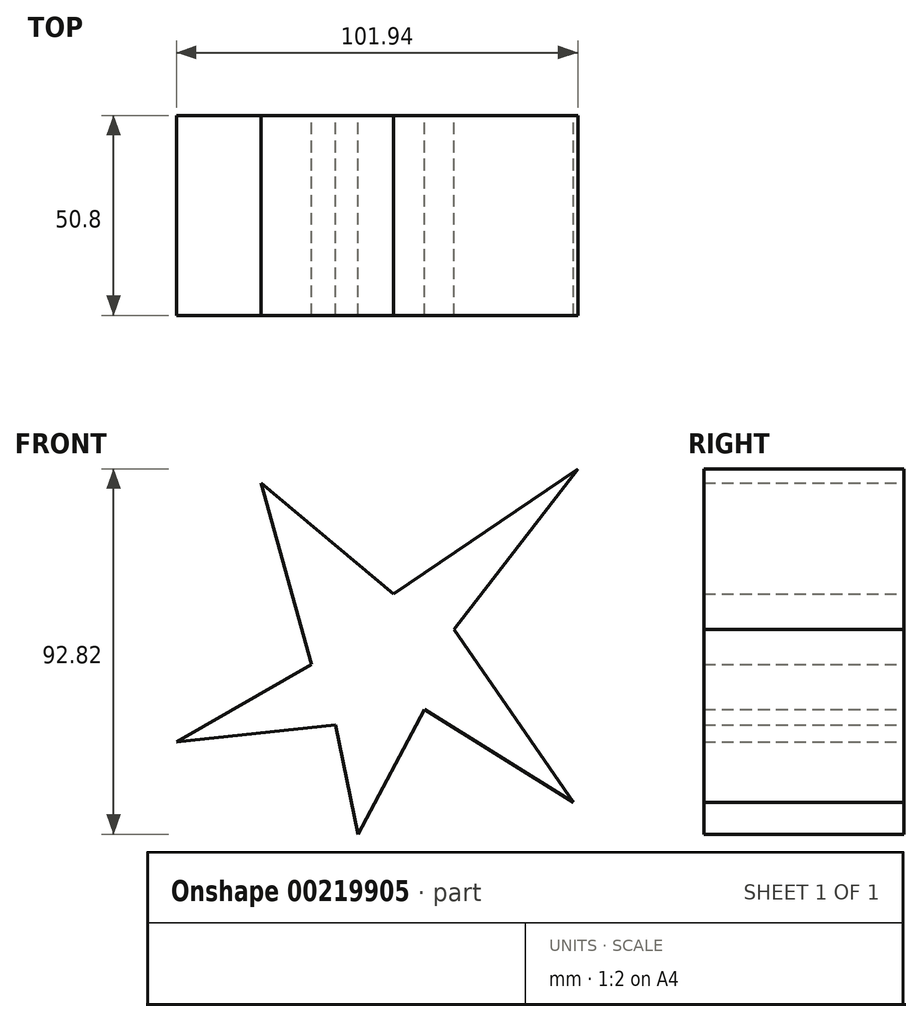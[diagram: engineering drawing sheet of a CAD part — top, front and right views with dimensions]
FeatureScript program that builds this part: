
annotation { "Feature Type Name" : "Feature", "Feature Type Description" : "" }
export const myFeature = defineFeature(function(context is Context, id is Id, definition is map)
    precondition{}
    {
        {
            var Q0;
            Q0=qCreatedBy(makeId("Front.planeOp"),FACE);
            var sketch = newSketch(context, id + "F0", { "sketchPlane" : qUnion([Q0])});
            skLineSegment(sketch, "E0", {"start": v(0, 0) * mm, "end": v(16.81, 31.66) * mm});
            skLineSegment(sketch, "E1", {"start": v(16.81, 31.66) * mm, "end": v(54.73, 8.05) * mm});
            skLineSegment(sketch, "E2", {"start": v(54.73, 8.05) * mm, "end": v(24.32, 52.04) * mm});
            skLineSegment(sketch, "E3", {"start": v(24.32, 52.04) * mm, "end": v(55.8, 92.82) * mm});
            skLineSegment(sketch, "E4", {"start": v(55.8, 92.82) * mm, "end": v(8.94, 60.99) * mm});
            skLineSegment(sketch, "E5", {"start": v(8.94, 60.99) * mm, "end": v(-24.68, 89.24) * mm});
            skLineSegment(sketch, "E6", {"start": v(-24.68, 89.24) * mm, "end": v(-11.8, 43.1) * mm});
            skLineSegment(sketch, "E7", {"start": v(-11.8, 43.1) * mm, "end": v(-46.14, 23.43) * mm});
            skLineSegment(sketch, "E8", {"start": v(-46.14, 23.43) * mm, "end": v(-5.72, 27.72) * mm});
            skLineSegment(sketch, "E9", {"start": v(-5.72, 27.72) * mm, "end": v(0, 0) * mm});
            skSolve(sketch);
        }
        {
            var Q0;
            Q0=makeQuery(id+"F0.imprint","IMPRINT",FACE,{"disambiguationData":[TD([[makeQuery(id+"F0.imprint","IMPRINT",EDGE,{"derivedFrom":sQuery(id+"F0.wireOp",EDGE,"E0")}),1.0]])]});
            extrude(context, id + "F1", {"entities" : qUnion([Q0]), "depth" : 50.8 * mm});
        }
    });
